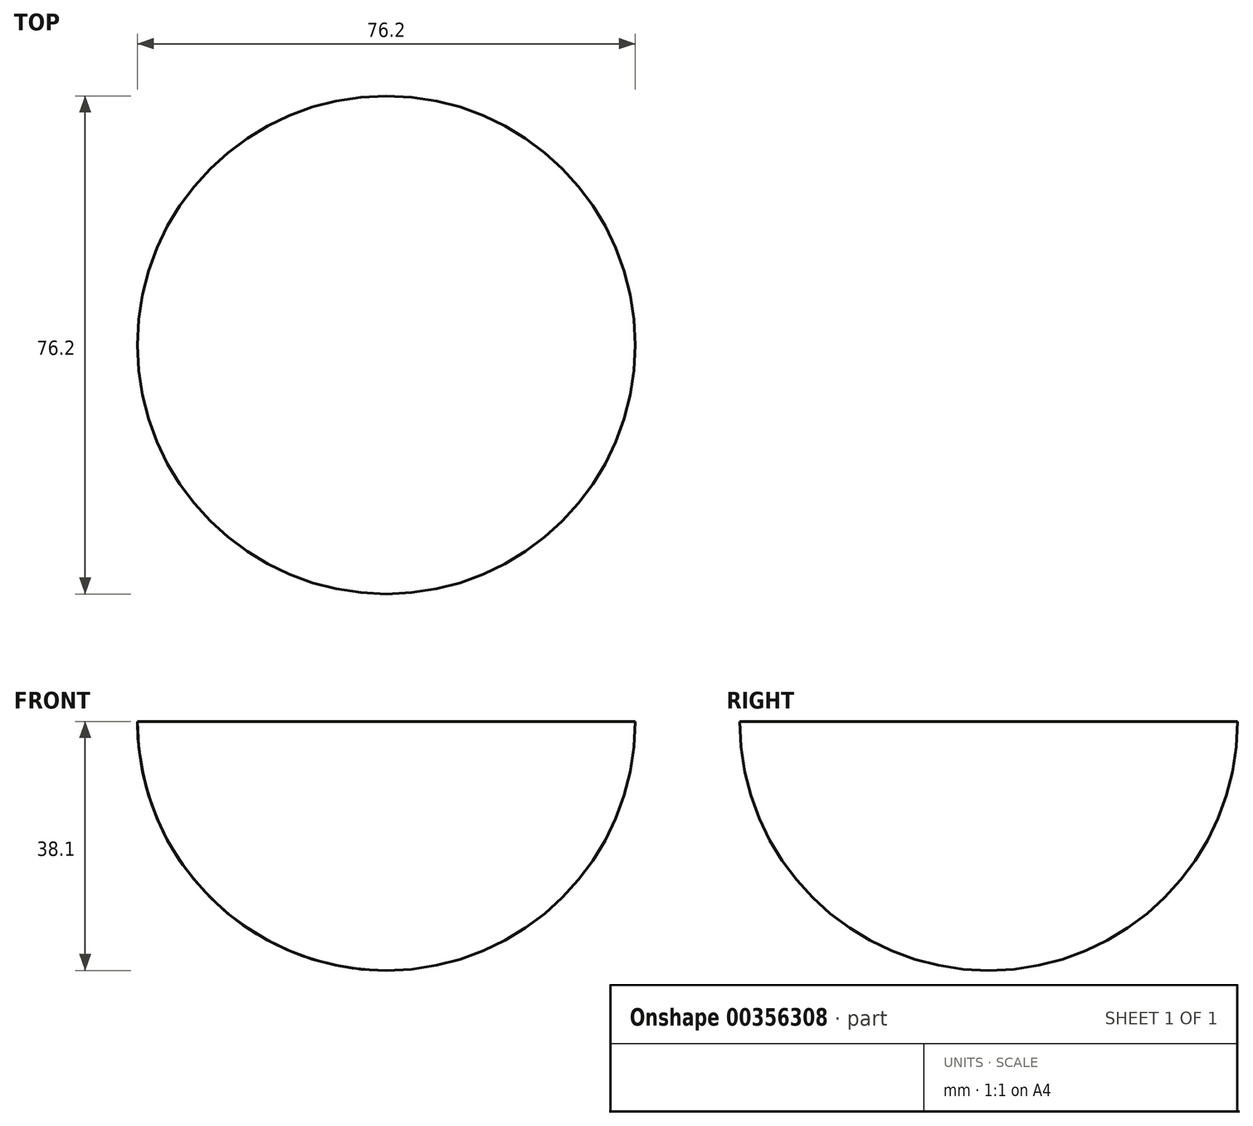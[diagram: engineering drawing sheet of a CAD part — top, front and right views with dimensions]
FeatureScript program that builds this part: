
annotation { "Feature Type Name" : "Feature", "Feature Type Description" : "" }
export const myFeature = defineFeature(function(context is Context, id is Id, definition is map)
    precondition{}
    {
        {
            var Q0;
            Q0=qCreatedBy(makeId("Front.planeOp"),FACE);
            var sketch = newSketch(context, id + "F0", { "sketchPlane" : qUnion([Q0])});
            skLineSegment(sketch, "E0", {"start": v(0, 0) * mm, "end": v(0, -38.1) * mm});
            skArc(sketch, "E1", {"start": v(0, -38.1) * mm, "mid": v(-26.94, -26.94) * mm, "end": v(-38.1, 0) * mm});
            skLineSegment(sketch, "E2", {"start": v(-38.1, 0) * mm, "end": v(0, 0) * mm});
            skSolve(sketch);
        }
        {
            var Q0;
            Q0=qSketchRegion(id+"F0",true);
            var Q1;
            Q1=sQuery(id+"F0.wireOp",EDGE,"E0");
            revolve(context, id + "F1", {"entities" : qUnion([Q0]), "axis" : qUnion([Q1]), "revolveType" : RevolveType.FULL});
        }
    });
